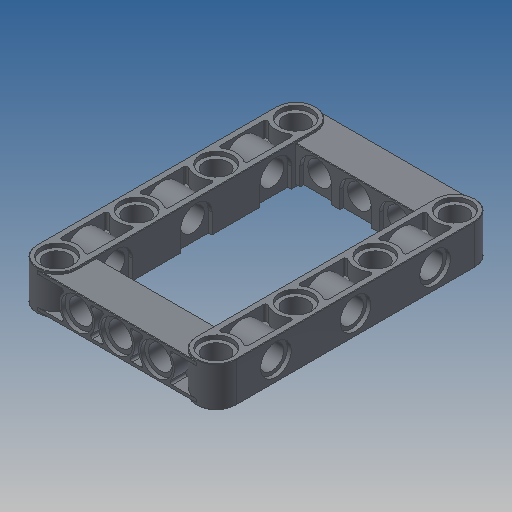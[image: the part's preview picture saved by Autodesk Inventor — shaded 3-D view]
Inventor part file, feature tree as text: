
AUTODESK INVENTOR PART (.ipt)
format: ipt  version: 2022.2 (Build 262287000, 287)  size: 812,032 bytes
history: native  units: mm
features: extrude x13, sketch x8, mirror x3, fillet x2, projected_geometry x2, plane x1
ambient origin geometry x8: Origin, YZ Plane, XZ Plane, XY Plane, X Axis, Y Axis, Z Axis, Center Point
bodies: Solid1 (feature_tree)
feature tree (29):
  extrude  "Extrusion1"  Depth=0.8mm TaperAngle=0.0deg
  sketch  "Sketch6"  dims[d14=8.0mm d15=0.0mm d41=0.8mm d42=0.0mm]
  extrude  "Extrusion7"  Depth=3.1mm
  extrude  "Extrusion8"  Depth=4.8mm
  extrude  "Extrusion19"  Depth=0.4mm
  mirror  "Mirror5"
  sketch  "Sketch7"  dims[d43=3.1mm d44=0.0mm d48=48.0mm]
  extrude  "Extrusion9"  Depth=10.0mm
  extrude  "Extrusion10"  Depth=10.0mm TaperAngle=0.0deg
  extrude  "Extrusion11"  Depth=10.0mm
  extrude  "Extrusion18"  [1 undecoded]
  fillet  "Fillet2"  Radius=8.0mm
  plane  "Work Plane1"
  extrude  "Extrusion13"  Depth=3.1mm
  sketch  "Sketch12"  dims[d62=30.0mm d64=16.0mm d65=10.0mm d67=10.0mm d69=7.2mm]
  extrude  "Extrusion14"  Depth=5.8mm
  extrude  "Extrusion15"  Depth=3.1mm
  extrude  "Extrusion16"  Depth=3.1mm TaperAngle=0.0deg
  extrude  "Extrusion17"  Depth=3.1mm
  fillet  "Fillet3"  Radius=6.4mm
  mirror  "Mirror4"
  mirror  "Mirror3"
  projected_geometry  "Projected Loop4"
  sketch  "Sketch8"  dims[d49=6.4mm d50=4.8mm]
  sketch  "Sketch11"  dims[d51=16.0mm d60=0.4mm d61=0.1mm]
  projected_geometry  "Projected Loop5"
  sketch  "Sketch13"  dims[d70=4.8mm d71=10.0mm d72=0.0mm]
  sketch  "Sketch14"  dims[d73=10.0mm d74=0.0mm d75=6.2mm]
  sketch  "Sketch15"  dims[d76=0.8mm d77=0.0mm d78=-16.0mm d86=8.0mm d87=3.1mm d88=5.8mm d89=7.2mm d90=0.9mm d91=0.0mm d92=4.8mm d93=6.4mm d94=0.9mm d95=0.0mm d96=0.9mm d97=0.0mm d98=0.8mm d99=0.0mm d100=6.4mm d101=0.8mm d102=0.0mm d103=0.1mm d104=0.4mm d106=6.4mm d107=0.8mm d108=0.0mm d109=45.0deg d111=1.6mm d112=3.1mm d113=0.0mm d114=16.0mm d116=45.0deg d117=56.0mm d118=8.0mm]
note: 1 required parameter value undecoded (feature->parameter linkage not recoverable at this tier; creation-order binding heuristic only, values carry confidence <= 0.55)
